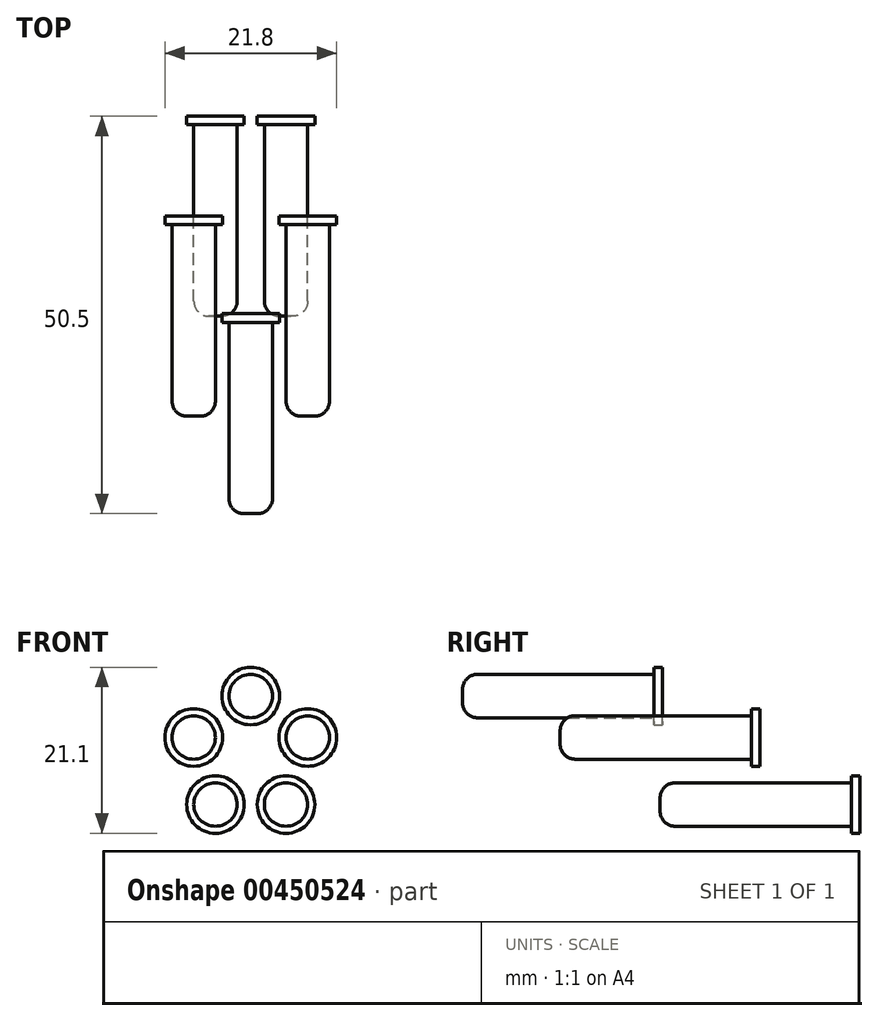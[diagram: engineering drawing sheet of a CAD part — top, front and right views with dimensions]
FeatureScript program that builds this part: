
annotation { "Feature Type Name" : "Feature", "Feature Type Description" : "" }
export const myFeature = defineFeature(function(context is Context, id is Id, definition is map)
    precondition{}
    {
        {
            var Q0;
            Q0=qCreatedBy(makeId("Front.planeOp"),FACE);
            var sketch = newSketch(context, id + "F0", { "sketchPlane" : qUnion([Q0])});
            skCircle(sketch, "E0", {"center": v(0, 7.62) * mm, "radius": 3.66 * mm});
            skCircle(sketch, "E1", {"center": v(0, 7.62) * mm, "radius": 2.76 * mm});
            skSolve(sketch);
        }
        {
            var Q0;
            Q0=makeQuery(id+"F0.imprint","IMPRINT",FACE,{"disambiguationData":[TD([[makeQuery(id+"F0.imprint","IMPRINT",EDGE,{"derivedFrom":sQuery(id+"F0.wireOp",EDGE,"E1")}),1.0]])]});
            extrude(context, id + "F1", {"entities" : qUnion([Q0]), "depth" : 25.4 * mm});
        }
        {
            var Q0;
            Q0=makeQuery(id+"F0.imprint","IMPRINT",FACE,{"disambiguationData":[TD([[makeQuery(id+"F0.imprint","IMPRINT",EDGE,{"derivedFrom":sQuery(id+"F0.wireOp",EDGE,"E0")}),1.0]])]});
            extrude(context, id + "F2", {"entities" : qUnion([Q0]), "operationType" : NewBodyOperationType.ADD, "depth" : 1.1 * mm});
        }
        {
            var Q0;
            Q0=makeQuery(id+"F1.opExtrude","CAP_EDGE",EDGE,{"disambiguationData":[OSD([sQuery(id+"F0.wireOp",EDGE,"E1")])],"isStart":false});
            fillet(context, id + "F3", {"entities" : qUnion([Q0]), "radius" : 1.9 * mm, "tangentPropagation" : true, "allowEdgeOverflow" : false});
        }
        {
            var Q0;
            Q0=qCreatedBy(makeId("Top.planeOp"),FACE);
            var sketch = newSketch(context, id + "F4", { "sketchPlane" : qUnion([Q0])});
            skLineSegment(sketch, "E2", {"start": v(0, 0) * mm, "end": v(0, -25.4) * mm});
            skSolve(sketch);
        }
        {
            var Q0;
            Q0=makeQuery(id+"F1.opExtrude","SWEPT_BODY",BODY,{"disambiguationData":[OSD([sQuery(id+"F0.wireOp",EDGE,"E1")])]});
            var Q1;
            Q1=sQuery(id+"F4.wireOp",EDGE,"E2");
            circularPattern(context, id + "F5", {"entities" : qUnion([Q0]), "axis" : qUnion([Q1]), "angle" : 360 * degree, "instanceCount" : 5, "equalSpace" : true, "computeTransformsWithoutBuiltin" : true});
        }
        {
            var Q0;
            Q0=makeQuery(id+"F5.opPattern","COPY",BODY,{"derivedFrom":makeQuery(id+"F1.opExtrude","SWEPT_BODY",BODY,{"disambiguationData":[OSD([sQuery(id+"F0.wireOp",EDGE,"E1")])]}),"instanceName":"4"});
            var Q1;
            Q1=makeQuery(id+"F5.opPattern","COPY",BODY,{"derivedFrom":makeQuery(id+"F1.opExtrude","SWEPT_BODY",BODY,{"disambiguationData":[OSD([sQuery(id+"F0.wireOp",EDGE,"E1")])]}),"instanceName":"1"});
            transform(context, id + "F6", {"entities" : qUnion([Q0, Q1]), "transformType" : TransformType.TRANSLATION_3D, "dx" : 0 * mm, "dy" : 12.4 * mm, "dz" : 0 * mm, "makeCopy" : false});
        }
        {
            var Q0;
            Q0=makeQuery(id+"F5.opPattern","COPY",BODY,{"derivedFrom":makeQuery(id+"F1.opExtrude","SWEPT_BODY",BODY,{"disambiguationData":[OSD([sQuery(id+"F0.wireOp",EDGE,"E1")])]}),"instanceName":"2"});
            var Q1;
            Q1=makeQuery(id+"F5.opPattern","COPY",BODY,{"derivedFrom":makeQuery(id+"F1.opExtrude","SWEPT_BODY",BODY,{"disambiguationData":[OSD([sQuery(id+"F0.wireOp",EDGE,"E1")])]}),"instanceName":"3"});
            transform(context, id + "F7", {"entities" : qUnion([Q0, Q1]), "transformType" : TransformType.TRANSLATION_3D, "dx" : 0 * mm, "dy" : 25.1 * mm, "dz" : 0 * mm, "makeCopy" : false});
        }
    });
